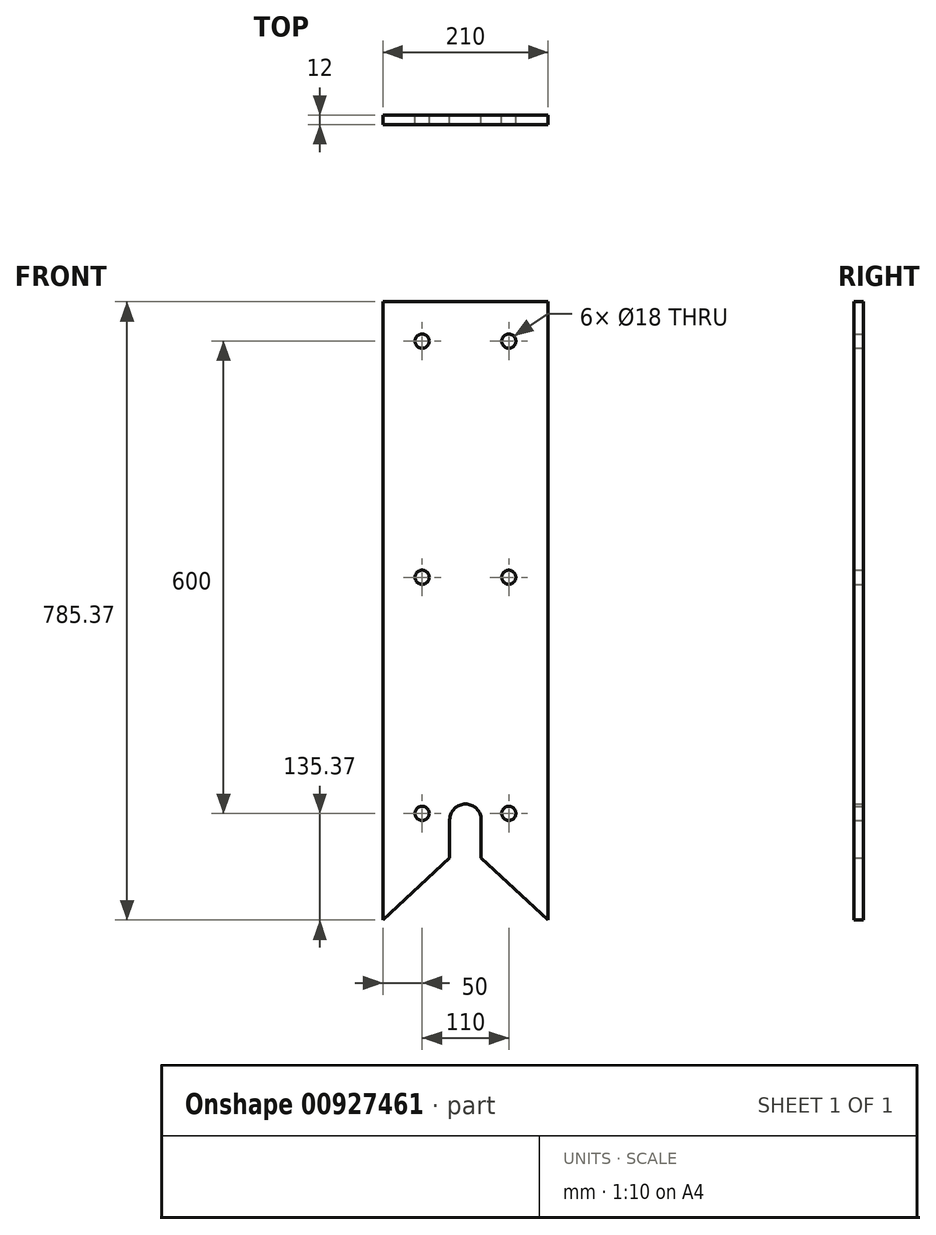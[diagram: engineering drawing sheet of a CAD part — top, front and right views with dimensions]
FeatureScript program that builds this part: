
annotation { "Feature Type Name" : "Feature", "Feature Type Description" : "" }
export const myFeature = defineFeature(function(context is Context, id is Id, definition is map)
    precondition{}
    {
        {
            var Q0;
            Q0=qCreatedBy(makeId("Front.planeOp"),FACE);
            var sketch = newSketch(context, id + "F0", { "sketchPlane" : qUnion([Q0])});
            skLineSegment(sketch, "E0", {"start": v(320, 0) * mm, "end": v(530, 0) * mm});
            skLineSegment(sketch, "E1", {"start": v(320, 0) * mm, "end": v(320, -785.37) * mm});
            skLineSegment(sketch, "E2", {"start": v(530, 0) * mm, "end": v(530, -785.37) * mm});
            skLineSegment(sketch, "E3", {"start": v(405, -658.09) * mm, "end": v(405, -706.62) * mm});
            skLineSegment(sketch, "E4", {"start": v(445, -658.09) * mm, "end": v(445, -706.62) * mm});
            skArc(sketch, "E5", {"start": v(405, -658.09) * mm, "mid": v(425, -638.09) * mm, "end": v(445, -658.09) * mm});
            skLineSegment(sketch, "E6", {"start": v(320, -785.37) * mm, "end": v(405, -706.62) * mm});
            skLineSegment(sketch, "E7", {"start": v(445, -706.62) * mm, "end": v(530, -785.37) * mm});
            skPoint(sketch, "E8", {"position": v(370, -50) * mm});
            skPoint(sketch, "E9", {"position": v(480, -50) * mm});
            skPoint(sketch, "E10", {"position": v(370, -350) * mm});
            skPoint(sketch, "E11", {"position": v(480, -350) * mm});
            skPoint(sketch, "E12", {"position": v(370, -650) * mm});
            skPoint(sketch, "E13", {"position": v(480, -650) * mm});
            skCircle(sketch, "E14", {"center": v(370, -50) * mm, "radius": 9 * mm});
            skCircle(sketch, "E15", {"center": v(480, -50) * mm, "radius": 9 * mm});
            skCircle(sketch, "E16", {"center": v(370, -350) * mm, "radius": 9 * mm});
            skCircle(sketch, "E17", {"center": v(480, -350) * mm, "radius": 9 * mm});
            skCircle(sketch, "E18", {"center": v(370, -650) * mm, "radius": 9 * mm});
            skCircle(sketch, "E19", {"center": v(480, -650) * mm, "radius": 9 * mm});
            skSolve(sketch);
        }
        {
            var Q0;
            Q0=makeQuery(id+"F0.imprint","IMPRINT",FACE,{"disambiguationData":[TD([[makeQuery(id+"F0.imprint","IMPRINT",EDGE,{"derivedFrom":sQuery(id+"F0.wireOp",EDGE,"E0")}),-1.0]])]});
            extrude(context, id + "F1", {"entities" : qUnion([Q0]), "depth" : 12 * mm, "offsetDistance" : 25 * mm});
        }
    });
